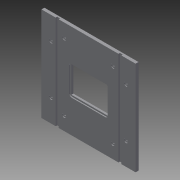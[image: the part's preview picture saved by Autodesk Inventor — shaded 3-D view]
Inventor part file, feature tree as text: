
AUTODESK INVENTOR PART (.ipt)
format: ipt  version: 2013 (Build 170138000, 138)  size: 174,592 bytes
history: native  units: in
note: dims shown in document units (in); Inventor stores cm internally (conversion verified against a paired STEP export)
features: sketch x5, extrude x4, hole x1
ambient origin geometry x8: Origin, YZ Plane, XZ Plane, XY Plane, X Axis, Y Axis, Z Axis, Center Point
bodies: Solid1 (feature_tree)
feature tree (10):
  extrude  "Extrusion1"  Depth=24.0in
  hole  "Hole2"  [1 undecoded]
  extrude  "Extrusion2"  Depth=2.4375in
  extrude  "Extrusion3"  Depth=5.75in
  extrude  "Extrusion4"  Depth=0.375in
  sketch  "Sketch1"  dims[d0=24.0in d2=24.0in]
  sketch  "Sketch2"  dims[d3=0.75in d4=0.0in d5=0.375in]
  sketch  "Sketch3"  dims[d6=5.75in d7=2.4375in]
  sketch  "Sketch4"  dims[d15=0.375in d16=5.75in]
  sketch  "Sketch5"  dims[d17=2.438in d18=0.375in d19=2.438in d20=5.75in d21=0.375in d22=2.4375in d23=5.75in d24=0.375in d25=5.7812in d26=3.4375in d27=0.375in d28=5.7812in d29=3.4375in d30=0.375in d31=3.4375in d32=5.7812in d33=0.375in d34=5.7812in d35=3.4375in d36=0.375in d37=0.75in d38=1.0in d39=0.1875in d40=0.5635in d41=1.0in d42=0.8108in d43=9.25in d44=6.75in d45=0.75in d46=0.0in d47=0.75in d48=90.0deg d49=90.0deg d50=0.375in d51=0.375in d52=0.375in d53=0.375in d54=90.0deg d55=0.375in d56=0.375in d57=0.375in d58=0.375in d59=0.25in d60=0.0in d61=0.75in d62=4.0in d63=0.75in d64=4.0in d65=0.375in d66=0.0in]
note: 1 required parameter value undecoded (feature->parameter linkage not recoverable at this tier; creation-order binding heuristic only, values carry confidence <= 0.55)
